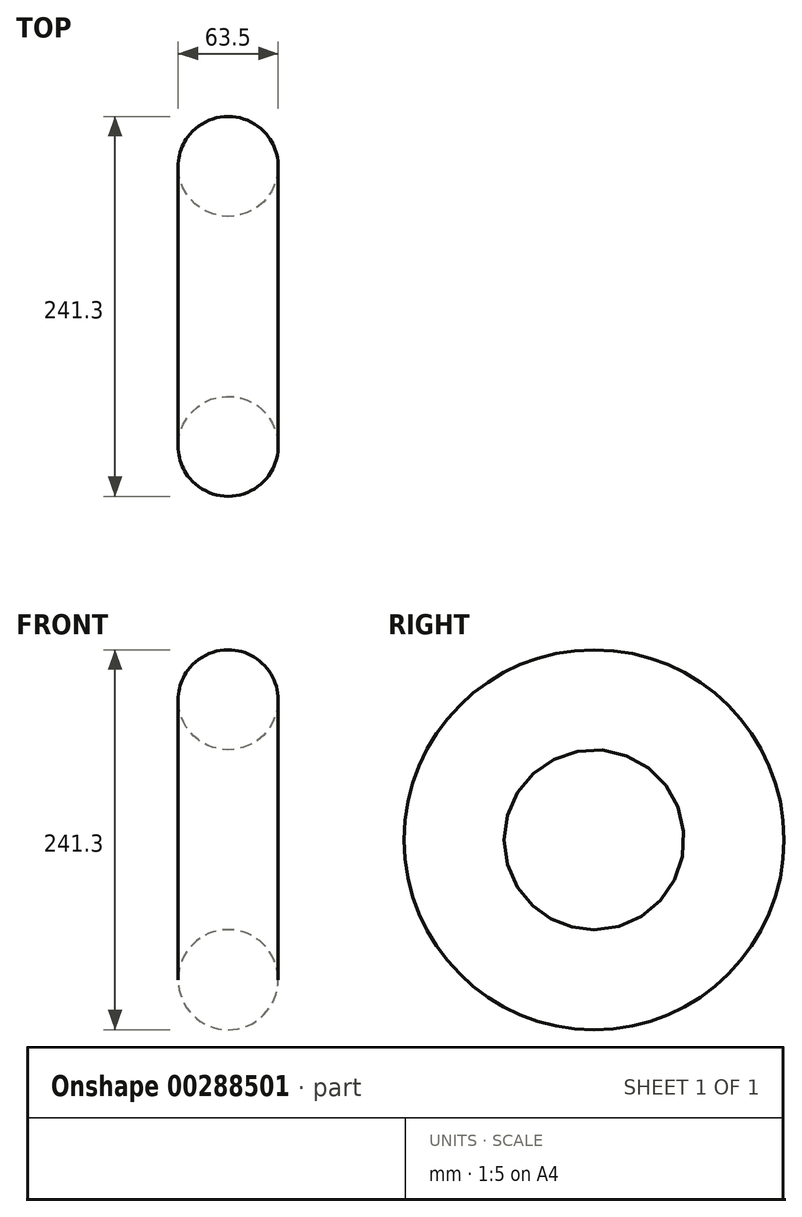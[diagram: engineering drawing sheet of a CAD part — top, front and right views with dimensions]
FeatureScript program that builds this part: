
annotation { "Feature Type Name" : "Feature", "Feature Type Description" : "" }
export const myFeature = defineFeature(function(context is Context, id is Id, definition is map)
    precondition{}
    {
        {
            var Q0;
            Q0=qCreatedBy(makeId("Front.planeOp"),FACE);
            var sketch = newSketch(context, id + "F0", { "sketchPlane" : qUnion([Q0])});
            skLineSegment(sketch, "E0", {"start": v(0, 0) * mm, "end": v(-76.57, 0) * mm, "construction": true});
            skCircle(sketch, "E1", {"center": v(0, 88.9) * mm, "radius": 31.75 * mm});
            skLineSegment(sketch, "E2", {"start": v(0, 0) * mm, "end": v(0, 115.6) * mm, "construction": true});
            skSolve(sketch);
        }
        {
            var Q0;
            Q0 = qSketchRegion(id + "F0", true);
            var Q1;
            Q1=sQuery(id+"F0.wireOp",EDGE,"E0");
            revolve(context, id + "F1", {"surfaceOperationType" : NewSurfaceOperationType.NEW, "entities" : qUnion([Q0]), "axis" : qUnion([Q1]), "revolveType" : RevolveType.FULL});
        }
    });
